# Revit family: CADS_AIRFLOWdev_FloorGrille_SatinStSteel140mm_Extract1
name_source: partatom
category: Air Terminals
revit_build: Autodesk Revit 2015 (Build: 20160512_1515(x64)
units: mm (PartAtom-declared; Revit-internal decimal feet)

## types (1)
- CADS_AIRFLOWdev_FloorGrille_SatinStSteel140mm_Extract
    6MonthlyMaintenance = Visually inspect system, clean the fan and ducting if necessary
    AssemblyPlace = UNKNOWN
    AssetType = FIXED
    CADS_Index = 0
    CEApproval = Yes
    Color = Silver
    Constituents = Floor Grille Satin Stainless Steel
    Default Elevation = 1219 mm
    DurationUnit = Year
    ExpectedServiceLife = 10
    Features = Satin Stainless Steel Floor Grille
    Finish = Lacquer
    FireControlPanelLinks = No
    Fitting Type = Ignore
    Grade = Stainless
    GrossWeight = 0.45 kg
    ISO140001 = Yes
    ISO90001 = Yes
    IsExtendedWarranty = No
    Manufacturer = Airflow Developments Ltd
    ManufacturerAddress = Aidelle House
Lancaster Road
Cressex Business Park
High Wycombe
Bucks
HP123QP
    ManufacturerTelephone = 01494 525252
    ManufacturerWebsite = www.airflow.com
    Material = Steel
    NBSCode = 90-75-50/370 Air terminals;
    NominalHeight = 37 mm  [stored 0.121391 ft]
    NominalLength = 161 mm  [stored 0.528215 ft]
    NominalWidth = 161 mm  [stored 0.528215 ft]
    PassiveHouseApproval = No
    PointOfContact = Airflow Developments Ltd
    ProductLiterature = https://www.airflow.com
    ProductionYear = 2017
    Quantity = 1
    RedDotDesignAward = No
    ReplacementCost = 78.744
    SAPApproval = Yes
    ServiceLifeDuration = 10
    ServiceLifeType = EXPECTEDSERVICELIFE
    Shape = Round
    ShippingWeight = 0.54 kg
    Size = 37 x 161 x 161
    Status = New
    TemperatureRange = up to 40°C
    Uniclass2015 = Pr_65_70_46_07
    WarrantyGuarantor = Airflow Developments Ltd
    WarrantyPeriod = 0

note: [stored X ft] marks values corroborated as IEEE doubles in the binary element streams (Revit-internal decimal feet)

## geometry (parser evidence)
native form markers: Sweep x2
no freeform markers — native parametric forms only
